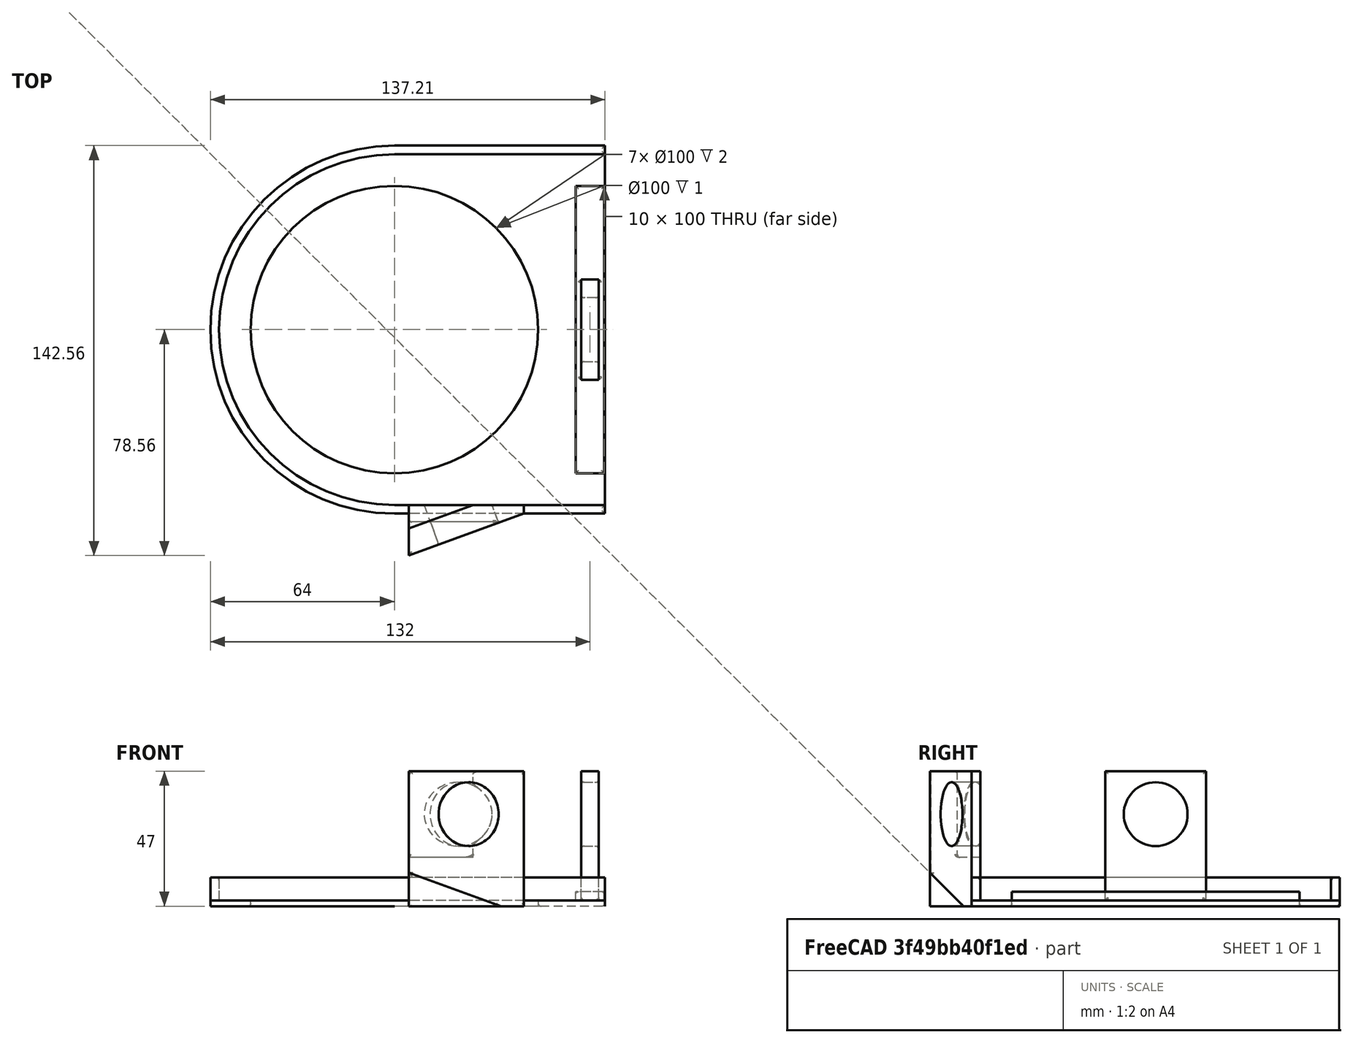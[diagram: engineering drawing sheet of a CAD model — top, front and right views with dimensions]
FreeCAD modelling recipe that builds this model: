
FCSTD DOCUMENT  (FreeCAD 0.16R)
Label: chainguard25T.04
License: All rights reserved
LicenseURL: http://en.wikipedia.org/wiki/All_rights_reserved
objects: Part::FeaturePython×17, Mesh::Feature×17, Sketcher::SketchObject×9, PartDesign::Fillet×8, PartDesign::Pad×5, PartDesign::Pocket×4
note: 52 computed .brp shape members not serialized (recipe doc carries the construction recipe); baked Part::Feature solids carry a one-line shape summary decoded from their .brp

FEATURE [Sketcher::SketchObject] Sketch001
  sketch-geometry (5):
    g0: LineSegment StartX=73.2073 StartY=64 StartZ=0 EndX=-2.4e-11 EndY=64 EndZ=0
    g1: LineSegment StartX=73.2073 StartY=-64 StartZ=0 EndX=3e-12 EndY=-64 EndZ=0
    g2: ArcOfCircle CenterX=-7.71025e-07 CenterY=0 CenterZ=0 NormalX=0 NormalY=0 NormalZ=1 Radius=64 StartAngle=1.5708 EndAngle=4.71239
    g3: LineSegment StartX=73.2073 StartY=64 StartZ=0 EndX=73.2073 EndY=-64 EndZ=0
    g4: Circle CenterX=0 CenterY=0 CenterZ=0 NormalX=0 NormalY=0 NormalZ=1 Radius=50
  constraints (13):
    c: Horizontal(g0)
    c: Horizontal(g1)
    c: Coincident(g2,g1)
    c: Coincident(g0,g2)
    c: DistanceX(g1,g0) = 0
    c: Equal(g0,g1)
    c: DistanceY(g1,g0) = 128
    c: Radius(g2) = 64
    c: Vertical(g3)
    c: Coincident(g1,g3)
    c: Symmetric(g1,g0,g-1)
    c: Radius(g4) = 50
    c: Coincident(g4,g-1)
FEATURE [PartDesign::Pad] Pad  label="Faceplate"
  Length = 2
  Length2 = 100
  Reversed = true
  Sketch = -> Sketch001
  Type = 0
FEATURE [Sketcher::SketchObject] Sketch002
  sketch-geometry (8):
    g0: LineSegment StartX=73.202 StartY=64 StartZ=0 EndX=0 EndY=64 EndZ=0
    g1: LineSegment StartX=73.202 StartY=-64 StartZ=0 EndX=0 EndY=-64 EndZ=0
    g2: ArcOfCircle CenterX=3.13138e-06 CenterY=0 CenterZ=0 NormalX=0 NormalY=0 NormalZ=1 Radius=64 StartAngle=1.5708 EndAngle=4.71239
    g3: LineSegment StartX=0 StartY=61 StartZ=0 EndX=73.202 EndY=61 EndZ=0
    g4: LineSegment StartX=0 StartY=-61 StartZ=0 EndX=73.202 EndY=-61 EndZ=0
    g5: LineSegment StartX=73.202 StartY=64 StartZ=0 EndX=73.202 EndY=61 EndZ=0
    g6: LineSegment StartX=73.202 StartY=-61 StartZ=0 EndX=73.202 EndY=-64 EndZ=0
    g7: ArcOfCircle CenterX=-7.37069e-05 CenterY=0 CenterZ=0 NormalX=0 NormalY=0 NormalZ=1 Radius=61 StartAngle=1.5708 EndAngle=4.71239
  constraints (25):
    c: Horizontal(g0)
    c: Horizontal(g1)
    c: Coincident(g2,g1)
    c: Coincident(g0,g2)
    c: DistanceX(g1,g0) = 0
    c: Equal(g0,g1)
    c: DistanceY(g1,g0) = 128
    c: Radius(g2) = 64
    c: Symmetric(g1,g0,g-1)
    c: Radius(g7) = 61
    c: Parallel(g0,g3)
    c: DistanceY(g3,g0) = 3
    c: DistanceY(g1,g4) = 3
    c: Parallel(g4,g1)
    c: DistanceX(g0,g3) = 0
    c: DistanceX(g4) = 0
    c: DistanceX(g0) = 73.202
    c: Equal(g3,g0)
    c: Equal(g4,g0)
    c: Coincident(g4,g6)
    c: Coincident(g6,g1)
    c: Coincident(g5,g3)
    c: Coincident(g5,g0)
    c: Coincident(g7,g3)
    c: Coincident(g7,g4)
FEATURE [PartDesign::Pad] Pad001  label="Connector"
  Length = 8
  Length2 = 100
  Sketch = -> Sketch002
  Type = 0
FEATURE [PartDesign::Fillet] Fillet  label="fillet_connector"
  Base = -> Pad001 [Edge4,Edge7,Edge10,Edge13,Edge16,Edge19,Edge22,Edge24]
  Radius = 1
FEATURE [PartDesign::Fillet] Fillet001  label="Fillet_face"
  Base = -> Pad [Edge4,Edge7,Edge10,Edge12,Edge15]
  Radius = 1
FEATURE [Sketcher::SketchObject] Sketch004  label="BossST"
  sketch-geometry (4):
    g0: LineSegment StartX=45 StartY=-61 StartZ=0 EndX=5 EndY=-61 EndZ=0
    g1: LineSegment StartX=5 StartY=-61 StartZ=0 EndX=5 EndY=-78.5588 EndZ=0
    g2: LineSegment StartX=45 StartY=-64 StartZ=0 EndX=45 EndY=-61 EndZ=0
    g3: LineSegment StartX=5 StartY=-78.5588 StartZ=0 EndX=45 EndY=-64 EndZ=0
  constraints (12):
    c: Coincident(g0,g1)
    c: Vertical(g1)
    c: Vertical(g2)
    c: DistanceX(g0,g0) = 40
    c: DistanceX(g-1,g1) = 5
    c: Angle(g3) = 0.349066
    c: DistanceY(g0,g-1) = 61
    c: Horizontal(g0)
    c: DistanceY(g2,g2) = 3
    c: Coincident(g2,g0)
    c: Coincident(g3,g2)
    c: Coincident(g1,g3)
FEATURE [PartDesign::Pad] Pad002  label="STboss"
  Length = 45
  Length2 = 2
  Sketch = -> Sketch004
  Type = 4
FEATURE [Sketcher::SketchObject] Sketch005
  Placement = pos=(25.8332,-70.9761,0) rot=(0.970288,0.171088,0.171088;1.60095rad)
  Support = -> Pad002 [Face3]
  sketch-geometry (1):
    g0: Circle CenterX=-0.0348267 CenterY=30 CenterZ=0 NormalX=0 NormalY=0 NormalZ=1 Radius=11.1
  constraints (2):
    c: Radius(g0) = 11.1
    c: DistanceY(g-1,g0) = 30
FEATURE [PartDesign::Pocket] Pocket  label="SThole"
  Length = 5
  Sketch = -> Sketch005
  Type = 1
FEATURE [Sketcher::SketchObject] Sketch006
  Placement = pos=(5,0,0) rot=(0.57735,-0.57735,-0.57735;2.0944rad)
  Support = -> Pocket [Face5]
  sketch-geometry (4):
    g0: LineSegment StartX=54.9217 StartY=-13.9475 StartZ=0 EndX=105.758 EndY=-27.5691 EndZ=0
    g1: LineSegment StartX=105.758 StartY=-27.5691 StartZ=0 EndX=92.1366 EndY=23.2674 EndZ=0
    g2: LineSegment StartX=92.1366 StartY=23.2674 StartZ=0 EndX=54.9217 EndY=-13.9475 EndZ=0
    g3: Circle [constr] CenterX=84.2722 CenterY=-6.08307 CenterZ=0 NormalX=0 NormalY=0 NormalZ=1 Radius=30.3858
  constraints (12):
    c: Coincident(g0,g1)
    c: Coincident(g1,g2)
    c: Coincident(g2,g0)
    c: Equal(g0,g1)
    c: Equal(g0,g2)
    c: PointOnObject(g0,g3)
    c: PointOnObject(g1,g3)
    c: PointOnObject(g2,g3)
    c: Angle(g2) = -2.35619
    c: Distance(g2) = 52.6298
    c: DistanceX(g-1,g0) = 54.9217
    c: DistanceY(g0,g-1) = 13.9475
FEATURE [PartDesign::Pocket] Pocket001  label="STpocket0"
  Length = 5
  Sketch = -> Sketch006
  Type = 1
FEATURE [Sketcher::SketchObject] Sketch007
  ExternalGeometry = -> [Pocket001]
  Placement = pos=(0,0,45) rot=(0,0,1;0rad)
  Support = -> Pocket001 [Face4]
  sketch-geometry (4):
    g0: LineSegment StartX=-4.66376 StartY=-54.3774 StartZ=0 EndX=-2.14442 EndY=-71.7516 EndZ=0
    g1: LineSegment StartX=-2.14442 StartY=-71.7516 StartZ=0 EndX=41.1328 EndY=-56 EndZ=0
    g2: LineSegment StartX=41.1328 StartY=-56 StartZ=0 EndX=37.1097 EndY=-55.1054 EndZ=0
    g3: LineSegment StartX=37.1097 StartY=-55.1054 StartZ=0 EndX=-4.66376 EndY=-54.3774 EndZ=0
  constraints (12):
    c: Coincident(g0,g1)
    c: Coincident(g1,g2)
    c: Coincident(g2,g3)
    c: Parallel(g1,g-3)
    c: DistanceY(g-3,g1) = 8
    c: Coincident(g0,g3)
    c: DistanceX(g1,g-3) = 3.86725
    c: Distance(g3) = 41.7798
    c: Distance(g0) = 17.5559
    c: Distance(g1) = 46.0546
    c: Distance(g2) = 4.12132
    c: DistanceX(g0,g-1) = 4.66376
FEATURE [PartDesign::Pocket] Pocket002  label="STpocket1"
  Length = 30
  Sketch = -> Sketch007
  Type = 0
FEATURE [Sketcher::SketchObject] Sketch008
  Support = -> Pad [Face6]
  sketch-geometry (4):
    g0: LineSegment StartX=65 StartY=17.5 StartZ=0 EndX=71 EndY=17.5 EndZ=0
    g1: LineSegment StartX=71 StartY=17.5 StartZ=0 EndX=71 EndY=-17.5 EndZ=0
    g2: LineSegment StartX=71 StartY=-17.5 StartZ=0 EndX=65 EndY=-17.5 EndZ=0
    g3: LineSegment StartX=65 StartY=-17.5 StartZ=0 EndX=65 EndY=17.5 EndZ=0
  constraints (12):
    c: Coincident(g0,g1)
    c: Coincident(g1,g2)
    c: Coincident(g2,g3)
    c: Coincident(g3,g0)
    c: Horizontal(g0)
    c: Horizontal(g2)
    c: Vertical(g1)
    c: Vertical(g3)
    c: Distance(g1) = 35
    c: Distance(g0) = 6
    c: DistanceY(g2,g-1) = 17.5
    c: DistanceX(g-1,g2) = 65
FEATURE [PartDesign::Pad] Pad003  label="SyncTubeBoss"
  Length = 45
  Length2 = 100
  Sketch = -> Sketch008
  Type = 0
FEATURE [Sketcher::SketchObject] Sketch009
  Placement = pos=(71,0,0) rot=(0.57735,0.57735,0.57735;2.0944rad)
  Support = -> Pad003 [Face9]
  sketch-geometry (1):
    g0: Circle CenterX=0 CenterY=30 CenterZ=0 NormalX=0 NormalY=0 NormalZ=1 Radius=11.1
  constraints (3):
    c: Radius(g0) = 11.1
    c: Distance(g-1,g0) = 30
    c: DistanceX(g-1,g0) = 0
FEATURE [PartDesign::Pocket] Pocket003  label="SyncTubeHole"
  Length = 5
  Sketch = -> Sketch009
  Type = 1
FEATURE [PartDesign::Fillet] Fillet002
  Base = -> Pocket003 [Edge25,Edge14,Edge26,Edge23,Edge27]
  Radius = 1
FEATURE [PartDesign::Fillet] Fillet003
  Base = -> Pocket002 [Edge27,Edge11,Edge26,Edge25,Edge15,Edge23]
  Radius = 1
FEATURE [PartDesign::Fillet] Fillet004
  Base = -> Fillet003 [Edge22,Edge23,Edge4,Edge13]
  Radius = 1
FEATURE [PartDesign::Fillet] Fillet005
  Base = -> Fillet004 [Edge52,Edge27,Edge55,Edge24,Edge54,Edge35]
  Radius = 1
FEATURE [PartDesign::Fillet] Fillet006
  Base = -> Fillet002 [Edge13,Edge3,Edge18,Edge19,Edge20]
  Radius = 1
FEATURE [Sketcher::SketchObject] Sketch
  Support = -> Pad [Face6]
  sketch-geometry (4):
    g0: LineSegment StartX=63 StartY=50 StartZ=0 EndX=73 EndY=50 EndZ=0
    g1: LineSegment StartX=73 StartY=50 StartZ=0 EndX=73 EndY=-50 EndZ=0
    g2: LineSegment StartX=73 StartY=-50 StartZ=0 EndX=63 EndY=-50 EndZ=0
    g3: LineSegment StartX=63 StartY=-50 StartZ=0 EndX=63 EndY=50 EndZ=0
  constraints (12):
    c: Coincident(g0,g1)
    c: Coincident(g1,g2)
    c: Coincident(g2,g3)
    c: Coincident(g3,g0)
    c: Horizontal(g0)
    c: Horizontal(g2)
    c: Vertical(g1)
    c: Vertical(g3)
    c: DistanceX(g0,g0) = 10
    c: DistanceY(g3,g3) = 100
    c: DistanceY(g-1,g0) = 50
    c: DistanceX(g-1,g0) = 63
FEATURE [PartDesign::Pad] Pad004  label="SyncBossStiffener"
  Length = 3
  Length2 = 100
  Sketch = -> Sketch
  Type = 0
FEATURE [PartDesign::Fillet] Fillet007  label="SyncBossFillet"
  Base = -> Pad004 [Edge26,Edge25,Edge23,Edge20]
  Radius = 1
FEATURE [Part::FeaturePython] refine  label="refine_Faceplate"  # WARN: FeaturePython — macro-defined, semantics opaque (R4)
  Base = -> Pad
FEATURE [Part::FeaturePython] refine001  label="refine_fillet_connector"  # WARN: FeaturePython — macro-defined, semantics opaque (R4)
  Base = -> Fillet
FEATURE [Part::FeaturePython] refine002  label="refine_SyncBossFillet"  # WARN: FeaturePython — macro-defined, semantics opaque (R4)
  Base = -> Fillet007
FEATURE [Part::FeaturePython] refine003  label="refine_SyncBossStiffener"  # WARN: FeaturePython — macro-defined, semantics opaque (R4)
  Base = -> Pad004
FEATURE [Part::FeaturePython] refine004  label="refine_Fillet006"  # WARN: FeaturePython — macro-defined, semantics opaque (R4)
  Base = -> Fillet006
FEATURE [Part::FeaturePython] refine005  label="refine_Fillet005"  # WARN: FeaturePython — macro-defined, semantics opaque (R4)
  Base = -> Fillet005
FEATURE [Part::FeaturePython] refine006  label="refine_Fillet004"  # WARN: FeaturePython — macro-defined, semantics opaque (R4)
  Base = -> Fillet004
FEATURE [Part::FeaturePython] refine007  label="refine_Fillet003"  # WARN: FeaturePython — macro-defined, semantics opaque (R4)
  Base = -> Fillet003
FEATURE [Part::FeaturePython] refine008  label="refine_Fillet002"  # WARN: FeaturePython — macro-defined, semantics opaque (R4)
  Base = -> Fillet002
FEATURE [Part::FeaturePython] refine009  label="refine_SyncTubeHole"  # WARN: FeaturePython — macro-defined, semantics opaque (R4)
  Base = -> Pocket003
FEATURE [Part::FeaturePython] refine010  label="refine_SyncTubeBoss"  # WARN: FeaturePython — macro-defined, semantics opaque (R4)
  Base = -> Pad003
FEATURE [Part::FeaturePython] refine011  label="refine_STpocket1"  # WARN: FeaturePython — macro-defined, semantics opaque (R4)
  Base = -> Pocket002
FEATURE [Part::FeaturePython] refine012  label="refine_STpocket0"  # WARN: FeaturePython — macro-defined, semantics opaque (R4)
  Base = -> Pocket001
FEATURE [Part::FeaturePython] refine013  label="refine_SThole"  # WARN: FeaturePython — macro-defined, semantics opaque (R4)
  Base = -> Pocket
FEATURE [Part::FeaturePython] refine014  label="refine_STboss"  # WARN: FeaturePython — macro-defined, semantics opaque (R4)
  Base = -> Pad002
FEATURE [Part::FeaturePython] refine015  label="refine_Fillet_face"  # WARN: FeaturePython — macro-defined, semantics opaque (R4)
  Base = -> Fillet001
FEATURE [Part::FeaturePython] refine016  label="refine_Connector"  # WARN: FeaturePython — macro-defined, semantics opaque (R4)
  Base = -> Pad001
FEATURE [Mesh::Feature] Mesh  label="refine_Faceplate (Meshed)"
FEATURE [Mesh::Feature] Mesh001  label="refine_fillet_connector (Meshed)"
FEATURE [Mesh::Feature] Mesh002  label="refine_SyncBossFillet (Meshed)"
FEATURE [Mesh::Feature] Mesh003  label="refine_SyncBossStiffener (Meshed)"
FEATURE [Mesh::Feature] Mesh004  label="refine_Fillet006 (Meshed)"
FEATURE [Mesh::Feature] Mesh005  label="refine_Fillet005 (Meshed)"
FEATURE [Mesh::Feature] Mesh006  label="refine_Fillet004 (Meshed)"
FEATURE [Mesh::Feature] Mesh007  label="refine_Fillet003 (Meshed)"
FEATURE [Mesh::Feature] Mesh008  label="refine_Fillet002 (Meshed)"
FEATURE [Mesh::Feature] Mesh009  label="refine_SyncTubeHole (Meshed)"
FEATURE [Mesh::Feature] Mesh010  label="refine_SyncTubeBoss (Meshed)"
FEATURE [Mesh::Feature] Mesh011  label="refine_STpocket1 (Meshed)"
FEATURE [Mesh::Feature] Mesh012  label="refine_STpocket0 (Meshed)"
FEATURE [Mesh::Feature] Mesh013  label="refine_SThole (Meshed)"
FEATURE [Mesh::Feature] Mesh014  label="refine_STboss (Meshed)"
FEATURE [Mesh::Feature] Mesh015  label="refine_Fillet_face (Meshed)"
FEATURE [Mesh::Feature] Mesh016  label="refine_Connector (Meshed)"
